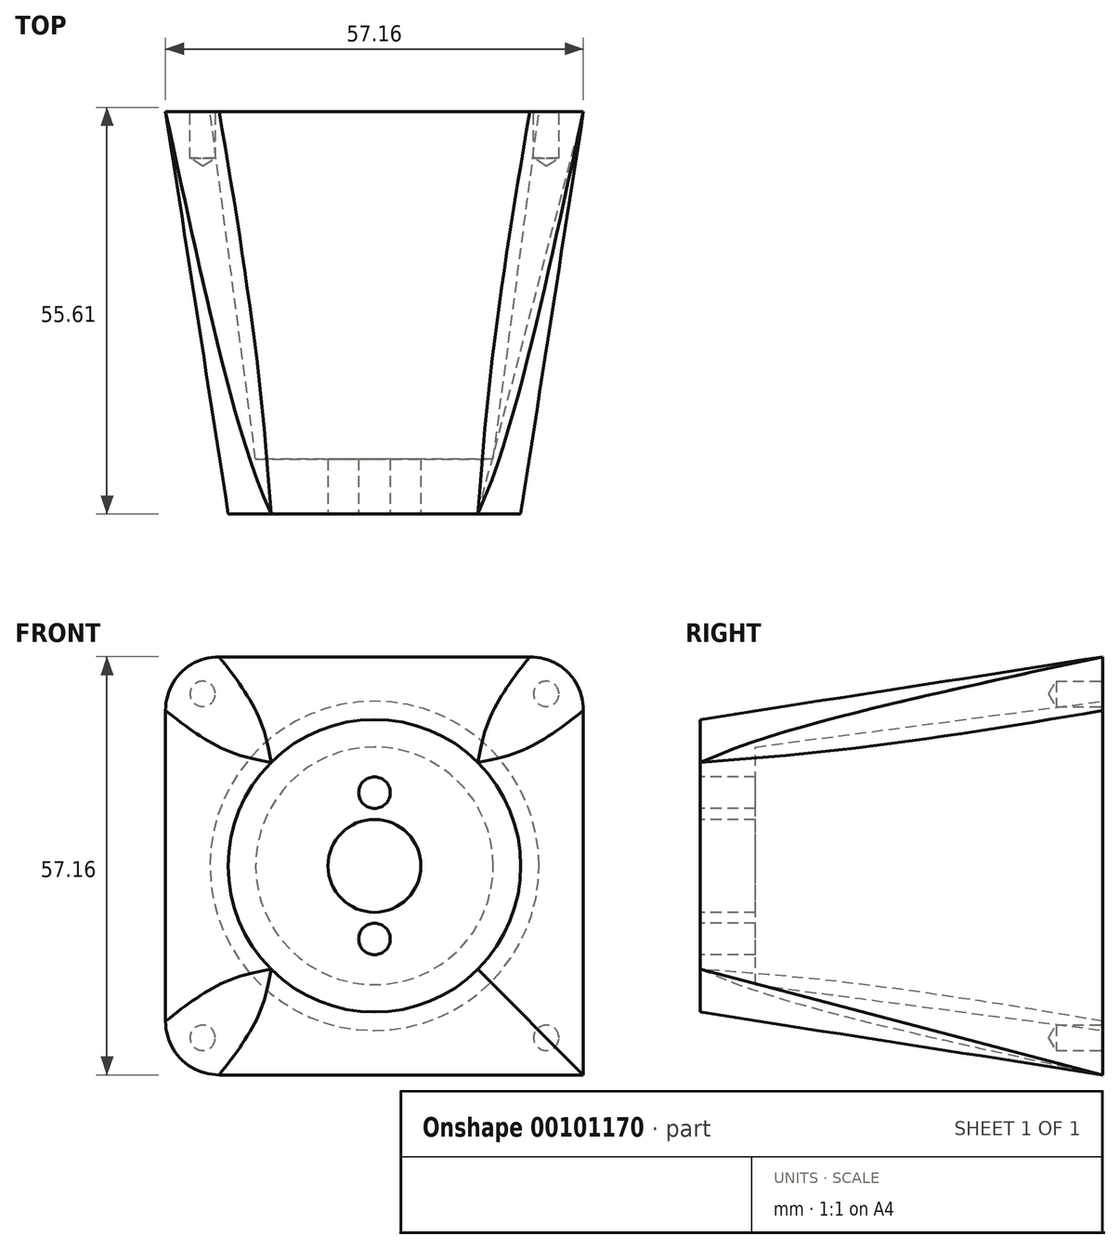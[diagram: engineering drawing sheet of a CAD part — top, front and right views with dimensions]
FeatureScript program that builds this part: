
annotation { "Feature Type Name" : "Feature", "Feature Type Description" : "" }
export const myFeature = defineFeature(function(context is Context, id is Id, definition is map)
    precondition{}
    {
        {
            var Q0;
            Q0=qCreatedBy(makeId("Front.planeOp"),FACE);
            var sketch = newSketch(context, id + "F0", { "sketchPlane" : qUnion([Q0])});
            skLineSegment(sketch, "E0.bottom", {"start": v(28.57, 28.58) * mm, "end": v(-28.58, 28.58) * mm});
            skLineSegment(sketch, "E0.top", {"start": v(28.58, -28.58) * mm, "end": v(-28.57, -28.58) * mm});
            skLineSegment(sketch, "E0.left", {"start": v(28.57, 28.58) * mm, "end": v(28.58, -28.58) * mm});
            skLineSegment(sketch, "E0.right", {"start": v(-28.58, 28.58) * mm, "end": v(-28.57, -28.58) * mm});
            skPoint(sketch, "E0.middle", {"position": v(0, 0) * mm});
            skLineSegment(sketch, "E1", {"start": v(-23.5, 23.5) * mm, "end": v(23.5, 23.5) * mm, "construction": true});
            skLineSegment(sketch, "E2", {"start": v(23.5, 23.5) * mm, "end": v(23.5, -23.5) * mm, "construction": true});
            skLineSegment(sketch, "E3", {"start": v(23.5, -23.5) * mm, "end": v(-23.5, -23.5) * mm, "construction": true});
            skLineSegment(sketch, "E4", {"start": v(-23.5, -23.5) * mm, "end": v(-23.5, 23.5) * mm, "construction": true});
            skLineSegment(sketch, "E5", {"start": v(-23.5, 23.5) * mm, "end": v(0, 0) * mm, "construction": true});
            skLineSegment(sketch, "E6", {"start": v(0, 0) * mm, "end": v(23.5, -23.5) * mm, "construction": true});
            skLineSegment(sketch, "E7", {"start": v(23.5, 23.5) * mm, "end": v(0, 0) * mm, "construction": true});
            skLineSegment(sketch, "E8", {"start": v(-23.5, -23.5) * mm, "end": v(0, 0) * mm, "construction": true});
            skPoint(sketch, "E9", {"position": v(-23.5, 23.5) * mm});
            skPoint(sketch, "E10", {"position": v(23.5, 23.5) * mm});
            skPoint(sketch, "E11", {"position": v(23.5, -23.5) * mm});
            skPoint(sketch, "E12", {"position": v(-23.5, -23.5) * mm});
            skSolve(sketch);
        }
        {
            var Q0;
            Q0=makeQuery(id+"F0.imprint","IMPRINT",FACE,{"disambiguationData":[TD([[makeQuery(id+"F0.imprint","IMPRINT",EDGE,{"derivedFrom":sQuery(id+"F0.wireOp",EDGE,"E0.bottom")}),1.0]])]});
            var sketch = newSketch(context, id + "F1", { "sketchPlane" : qUnion([Q0])});
            skPoint(sketch, "E13.middle", {"position": v(0, 0) * mm});
            skCircle(sketch, "E14", {"center": v(0, 0) * mm, "radius": 22.5 * mm});
            skSolve(sketch);
        }
        {
            var Q0;
            Q0=qCreatedBy(makeId("Front.planeOp"),FACE);
            cPlane(context, id + "F2", {"entities" : qUnion([Q0]), "cplaneType" : CPlaneType.OFFSET, "offset" : 55 * mm, "width" : 150 * mm, "height" : 150 * mm});
        }
        {
            var Q0;
            Q0=qCreatedBy(id+"F2.planeOp",FACE);
            var sketch = newSketch(context, id + "F3", { "sketchPlane" : qUnion([Q0])});
            skPoint(sketch, "E15", {"position": v(0, 10) * mm});
            skPoint(sketch, "E16", {"position": v(0, -10) * mm});
            skLineSegment(sketch, "E17", {"start": v(0, 10) * mm, "end": v(0, 0) * mm, "construction": true});
            skLineSegment(sketch, "E18", {"start": v(0, -10) * mm, "end": v(0, 0) * mm, "construction": true});
            skCircle(sketch, "E19", {"center": v(0, 0) * mm, "radius": 20 * mm});
            skSolve(sketch);
        }
        {
            var Q0;
            Q0=qCreatedBy(id+"F2.planeOp",FACE);
            cPlane(context, id + "F4", {"entities" : qUnion([Q0]), "cplaneType" : CPlaneType.OFFSET, "offset" : 7.5 * mm, "oppositeDirection" : true, "width" : 150 * mm, "height" : 150 * mm});
        }
        {
            var Q0;
            Q0=makeQuery(id+"F3.imprint","IMPRINT",FACE,{"disambiguationData":[TD([[makeQuery(id+"F3.imprint","IMPRINT",EDGE,{"derivedFrom":sQuery(id+"F3.wireOp",EDGE,"E19")}),1.0]])]});
            var Q1;
            Q1=makeQuery(id+"F0.imprint","IMPRINT",FACE,{"disambiguationData":[TD([[makeQuery(id+"F0.imprint","IMPRINT",EDGE,{"derivedFrom":sQuery(id+"F0.wireOp",EDGE,"E0.bottom")}),1.0]])]});
            loft(context, id + "F5", {"sheetProfilesArray" : [{ "sheetProfileEntities" : qUnion([Q0]) }, { "sheetProfileEntities" : qUnion([Q1]) }]});
        }
        {
            var Q0;
            Q0 = qSketchRegion(id + "F1", true);
            var Q1;
            Q1=sQuery(id+"F1.wireOp",EDGE,"E14");
            var Q2;
            Q2=qCreatedBy(id+"F4.planeOp",FACE);
            extrude(context, id + "F6", {"entities" : qUnion([Q0]), "operationType" : NewBodyOperationType.REMOVE, "surfaceEntities" : qUnion([Q1]), "endBound" : BoundingType.UP_TO_SURFACE, "endBoundEntityFace" : qUnion([Q2]), "depth" : 25 * mm, "hasDraft" : true, "draftAngle" : 7.5 * degree, "draftPullDirection" : true});
        }
        {
            var Q0;
            Q0=sQuery(id+"F3.wireOp",VERTEX,"E15");
            var Q1;
            Q1=sQuery(id+"F3.wireOp",VERTEX,"E16");
            var Q2;
            Q2=makeQuery(id+"F5.opLoft","SWEPT_BODY",BODY,{"disambiguationData":[OSD([makeQuery(id+"F0.imprint","IMPRINT",FACE,{"disambiguationData":[TD([[makeQuery(id+"F0.imprint","IMPRINT",EDGE,{"derivedFrom":sQuery(id+"F0.wireOp",EDGE,"E0.bottom")}),1.0]])]}),makeQuery(id+"F3.imprint","IMPRINT",FACE,{"disambiguationData":[TD([[makeQuery(id+"F3.imprint","IMPRINT",EDGE,{"derivedFrom":sQuery(id+"F3.wireOp",EDGE,"E19")}),1.0]])]})])]});
            hole(context, id + "F7", {"style" : HoleStyle.SIMPLE, "endStyle" : HoleEndStyle.THROUGH, "standardTappedOrClearance" : lookupTablePath({ "standard" : "ANSI", "fit" : "Close", "size" : "#8", "type" : "Clearance" }), "standardBlindInLast" : lookupTablePath({ "fit" : "Close", "standard" : "ANSI", "size" : "#8", "type" : "Clearance" }), "holeDiameter" : 4.32 * mm, "locations" : qUnion([Q0, Q1]), "scope" : qUnion([Q2]), "isTappedThrough" : true});
        }
        {
            var Q0;
            Q0=makeQuery(id+"F5.opLoft","SWEPT_EDGE",EDGE,{"disambiguationData":[OSD([sQuery(id+"F0.wireOp",EDGE,"E0.bottom"),sQuery(id+"F0.wireOp",EDGE,"E0.top"),sQuery(id+"F0.wireOp",EDGE,"E0.left"),sQuery(id+"F3.wireOp",EDGE,"E19")])]});
            var Q1;
            Q1=makeQuery(id+"F5.opLoft","SWEPT_EDGE",EDGE,{"disambiguationData":[OSD([sQuery(id+"F0.wireOp",EDGE,"E0.bottom"),sQuery(id+"F0.wireOp",EDGE,"E0.left")])]});
            var Q2;
            Q2=makeQuery(id+"F5.opLoft","SWEPT_EDGE",EDGE,{"disambiguationData":[OSD([sQuery(id+"F0.wireOp",EDGE,"E0.bottom"),sQuery(id+"F0.wireOp",EDGE,"E0.top"),sQuery(id+"F0.wireOp",EDGE,"E0.right"),sQuery(id+"F3.wireOp",EDGE,"E19")])]});
            var Q3;
            Q3=makeQuery(id+"F5.opLoft","SWEPT_EDGE",EDGE,{"disambiguationData":[OSD([sQuery(id+"F0.wireOp",EDGE,"E0.top"),sQuery(id+"F0.wireOp",EDGE,"E0.left"),sQuery(id+"F0.wireOp",EDGE,"E0.right"),sQuery(id+"F3.wireOp",EDGE,"E19")])]});
            fillet(context, id + "F8", {"entities" : qUnion([Q0, Q1, Q2, Q3]), "radius" : 7.5 * mm, "tangentPropagation" : true, "allowEdgeOverflow" : false});
        }
        {
            var Q0;
            Q0=sQuery(id+"F0.wireOp",VERTEX,"E9");
            var Q1;
            Q1=sQuery(id+"F0.wireOp",VERTEX,"E12");
            var Q2;
            Q2=sQuery(id+"F0.wireOp",VERTEX,"E11");
            var Q3;
            Q3=sQuery(id+"F0.wireOp",VERTEX,"E10");
            var Q4;
            Q4=makeQuery(id+"F5.opLoft","SWEPT_BODY",BODY,{"disambiguationData":[OSD([makeQuery(id+"F0.imprint","IMPRINT",FACE,{"disambiguationData":[TD([[makeQuery(id+"F0.imprint","IMPRINT",EDGE,{"derivedFrom":sQuery(id+"F0.wireOp",EDGE,"E0.bottom")}),1.0]])]}),makeQuery(id+"F3.imprint","IMPRINT",FACE,{"disambiguationData":[TD([[makeQuery(id+"F3.imprint","IMPRINT",EDGE,{"derivedFrom":sQuery(id+"F3.wireOp",EDGE,"E19")}),1.0]])]})])]});
            hole(context, id + "F9", {"style" : HoleStyle.SIMPLE, "endStyle" : HoleEndStyle.BLIND, "oppositeDirection" : true, "standardTappedOrClearance" : lookupTablePath({ "standard" : "ANSI", "engagement" : "75%", "pitch" : "32 tpi", "size" : "#8", "type" : "Tapped" }), "standardBlindInLast" : lookupTablePath({ "standard" : "ANSI", "engagement" : "75%", "pitch" : "32 tpi", "size" : "#8", "type" : "Tapped" }), "holeDiameter" : 3.45 * mm, "holeDepth" : 6.35 * mm, "locations" : qUnion([Q0, Q1, Q2, Q3]), "scope" : qUnion([Q4]), "majorDiameter" : 4.17 * mm});
        }
        {
            var Q0;
            Q0=makeQuery(id+"F3.imprint","IMPRINT",FACE,{"disambiguationData":[TD([[makeQuery(id+"F3.imprint","IMPRINT",EDGE,{"derivedFrom":sQuery(id+"F3.wireOp",EDGE,"E19")}),1.0]])]});
            var sketch = newSketch(context, id + "F10", { "sketchPlane" : qUnion([Q0])});
            skCircle(sketch, "E20", {"center": v(0, 0) * mm, "radius": 6.35 * mm});
            skSolve(sketch);
        }
        {
            var Q0;
            Q0 = qSketchRegion(id + "F10", true);
            var Q1;
            Q1=sQuery(id+"F10.wireOp",EDGE,"E20");
            extrude(context, id + "F11", {"entities" : qUnion([Q0]), "operationType" : NewBodyOperationType.REMOVE, "surfaceEntities" : qUnion([Q1]), "endBound" : BoundingType.THROUGH_ALL, "oppositeDirection" : true, "depth" : 25 * mm});
        }
    });
